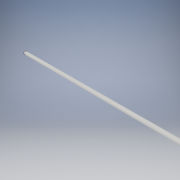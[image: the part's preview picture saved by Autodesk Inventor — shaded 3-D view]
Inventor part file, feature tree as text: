
AUTODESK INVENTOR PART (.ipt)
format: ipt  version: 2019 (Build 230136000, 136)  size: 89,600 bytes
history: native  units: in
note: dims shown in document units (in); Inventor stores cm internally (conversion verified against a paired STEP export)
features: extrude x1, sketch x1
ambient origin geometry x8: Origin, YZ Plane, XZ Plane, XY Plane, X Axis, Y Axis, Z Axis, Center Point
bodies: Solid1 (feature_tree)
feature tree (2):
  extrude  "Extrusion1"  Depth=24.0in TaperAngle=0.0deg
  sketch  "Sketch1"  dims[d0=0.5in d1=24.0in d2=0.0in]
